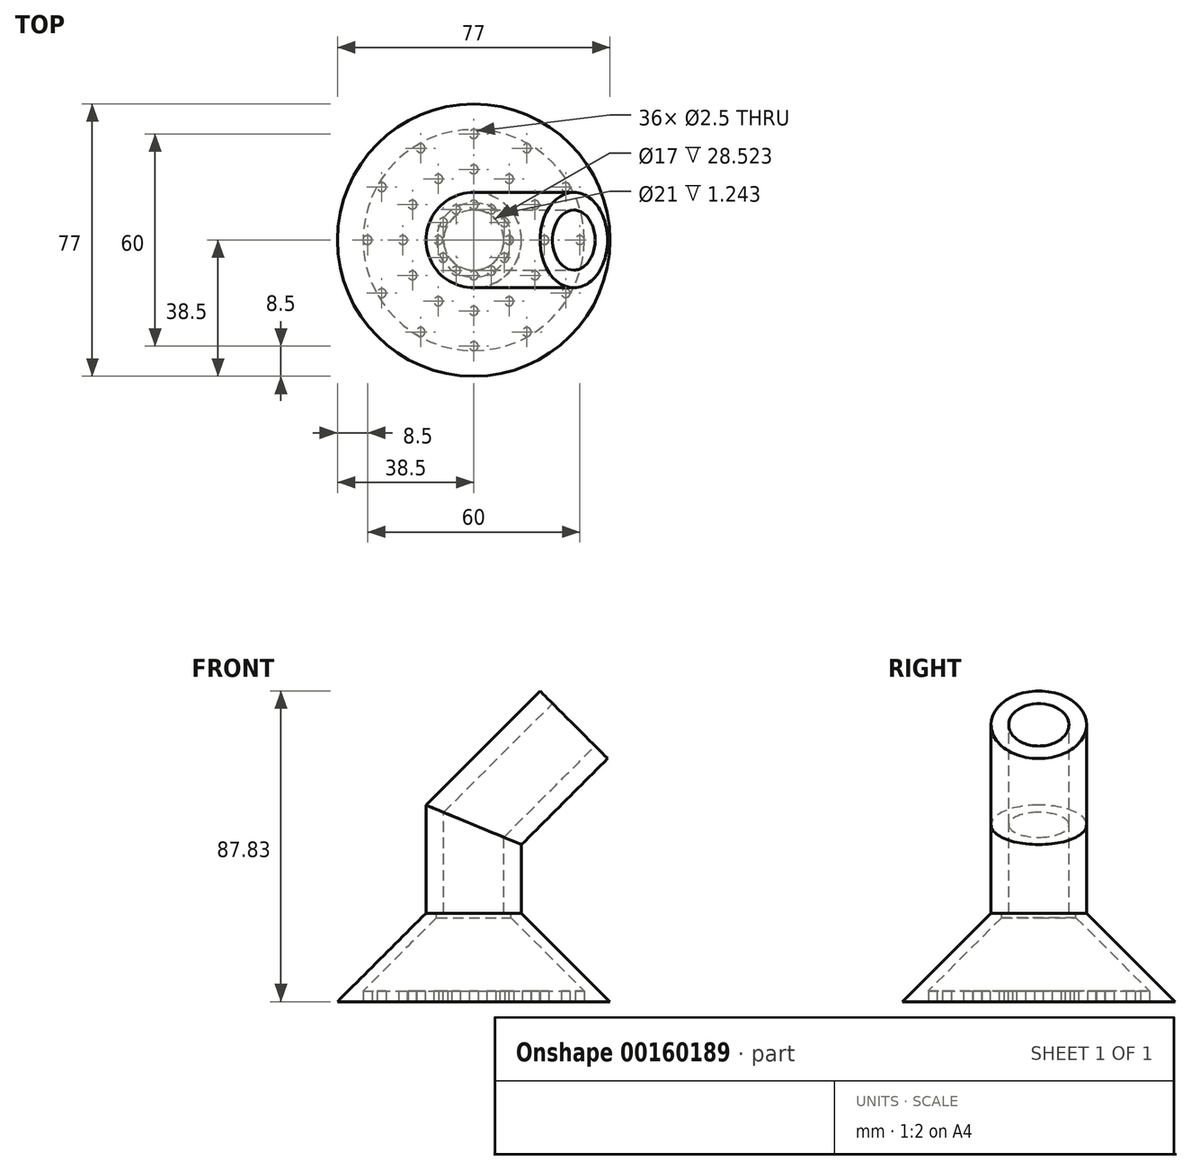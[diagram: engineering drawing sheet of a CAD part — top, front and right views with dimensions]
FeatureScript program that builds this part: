
annotation { "Feature Type Name" : "Feature", "Feature Type Description" : "" }
export const myFeature = defineFeature(function(context is Context, id is Id, definition is map)
    precondition{}
    {
        {
            var Q0;
            Q0=qCreatedBy(makeId("Top.planeOp"),FACE);
            var sketch = newSketch(context, id + "F0", { "sketchPlane" : qUnion([Q0])});
            skCircle(sketch, "E0", {"center": v(0, 0) * mm, "radius": 8.5 * mm});
            skCircle(sketch, "E1.0", {"center": v(0, 0) * mm, "radius": 13.5 * mm});
            skSolve(sketch);
        }
        {
            var Q0;
            Q0=qCreatedBy(makeId("Front.planeOp"),FACE);
            var sketch = newSketch(context, id + "F1", { "sketchPlane" : qUnion([Q0])});
            skLineSegment(sketch, "E2", {"start": v(0, 0) * mm, "end": v(0, 25) * mm});
            skLineSegment(sketch, "E3", {"start": v(0, 25) * mm, "end": v(28.28, 53.28) * mm});
            skSolve(sketch);
        }
        {
            var Q0;
            Q0=makeQuery(id+"F0.imprint","IMPRINT",FACE,{"disambiguationData":[TD([[makeQuery(id+"F0.imprint","IMPRINT",EDGE,{"derivedFrom":sQuery(id+"F0.wireOp",EDGE,"E0")}),-1.0]])]});
            var Q1;
            Q1=sQuery(id+"F1.wireOp",EDGE,"E2");
            var Q2;
            Q2=sQuery(id+"F1.wireOp",EDGE,"E3");
            sweep(context, id + "F10", {"profiles" : qUnion([Q0]), "path" : qUnion([Q1, Q2])});
        }
        {
            var Q0;
            Q0=makeQuery(id+"F10.opSweep","CAP_FACE",FACE,{"disambiguationData":[OSD([sQuery(id+"F0.wireOp",EDGE,"E0"),sQuery(id+"F0.wireOp",EDGE,"E1.0"),sQuery(id+"F1.wireOp",VERTEX,"E2.start")])],"isStart":true});
            var sketch = newSketch(context, id + "F11", { "sketchPlane" : qUnion([Q0])});
            skCircle(sketch, "E4", {"center": v(0, 0) * mm, "radius": 13.5 * mm});
            skSolve(sketch);
        }
        {
            var Q0;
            Q0 = qSketchRegion(id + "F11", true);
            extrude(context, id + "F2", {"entities" : qUnion([Q0]), "operationType" : NewBodyOperationType.ADD, "depth" : 25 * mm, "hasDraft" : true, "draftAngle" : 45 * degree});
        }
        {
            var Q0;
            Q0=makeQuery(id+"F2.opExtrude","CAP_FACE",FACE,{"disambiguationData":[OSD([sQuery(id+"F11.wireOp",EDGE,"E4")])],"isStart":true});
            shell(context, id + "F3", {"entities" : qUnion([Q0]), "thickness" : 3 * mm});
        }
        {
            var Q0;
            Q0=makeQuery(id+"F2.opExtrude","CAP_FACE",FACE,{"disambiguationData":[OSD([sQuery(id+"F11.wireOp",EDGE,"E4")])],"isStart":false});
            var sketch = newSketch(context, id + "F4", { "sketchPlane" : qUnion([Q0])});
            skPoint(sketch, "E5", {"position": v(-10, 0) * mm});
            skPoint(sketch, "E6", {"position": v(-20, 0) * mm});
            skPoint(sketch, "E7", {"position": v(-30, 0) * mm});
            skPoint(sketch, "E8.center", {"position": v(0, 0) * mm});
            skCircle(sketch, "E9", {"center": v(-10, 0) * mm, "radius": 1.25 * mm});
            skCircle(sketch, "E10", {"center": v(-20, 0) * mm, "radius": 1.25 * mm});
            skCircle(sketch, "E11", {"center": v(-30, 0) * mm, "radius": 1.25 * mm});
            skSolve(sketch);
        }
        {
            var Q0;
            Q0=makeQuery(id+"F4.imprint","IMPRINT",FACE,{"disambiguationData":[TD([[makeQuery(id+"F4.imprint","IMPRINT",EDGE,{"derivedFrom":sQuery(id+"F4.wireOp",EDGE,"E9")}),1.0]])]});
            extrude(context, id + "F5", {"entities" : qUnion([Q0]), "endBound" : BoundingType.UP_TO_NEXT, "oppositeDirection" : true, "depth" : 25 * mm});
        }
        {
            var Q0;
            Q0=makeQuery(id+"F4.imprint","IMPRINT",FACE,{"disambiguationData":[TD([[makeQuery(id+"F4.imprint","IMPRINT",EDGE,{"derivedFrom":sQuery(id+"F4.wireOp",EDGE,"E10")}),1.0]])]});
            extrude(context, id + "F6", {"entities" : qUnion([Q0]), "endBound" : BoundingType.UP_TO_NEXT, "oppositeDirection" : true, "depth" : 25 * mm});
        }
        {
            var Q0;
            Q0=makeQuery(id+"F4.imprint","IMPRINT",FACE,{"disambiguationData":[TD([[makeQuery(id+"F4.imprint","IMPRINT",EDGE,{"derivedFrom":sQuery(id+"F4.wireOp",EDGE,"E11")}),1.0]])]});
            extrude(context, id + "F12", {"entities" : qUnion([Q0]), "endBound" : BoundingType.UP_TO_NEXT, "oppositeDirection" : true, "depth" : 25 * mm});
        }
        {
            var Q0;
            Q0=makeQuery(id+"F5.opExtrude","SWEPT_BODY",BODY,{"disambiguationData":[OSD([sQuery(id+"F4.wireOp",EDGE,"E9")])]});
            var Q1;
            Q1=makeQuery(id+"F2.opExtrude","CAP_EDGE",EDGE,{"disambiguationData":[OSD([sQuery(id+"F11.wireOp",EDGE,"E4")])],"isStart":false});
            circularPattern(context, id + "F7", {"operationType" : NewBodyOperationType.REMOVE, "entities" : qUnion([Q0]), "axis" : qUnion([Q1]), "angle" : 30 * degree, "instanceCount" : 15, "oppositeDirection" : true});
        }
        {
            var Q0;
            Q0=makeQuery(id+"F6.opExtrude","SWEPT_BODY",BODY,{"disambiguationData":[OSD([sQuery(id+"F4.wireOp",EDGE,"E10")])]});
            var Q1;
            Q1=makeQuery(id+"F2.opExtrude","CAP_EDGE",EDGE,{"disambiguationData":[OSD([sQuery(id+"F11.wireOp",EDGE,"E4")])],"isStart":false});
            circularPattern(context, id + "F8", {"operationType" : NewBodyOperationType.REMOVE, "entities" : qUnion([Q0]), "axis" : qUnion([Q1]), "angle" : 30 * degree, "instanceCount" : 15});
        }
        {
            var Q0;
            Q0=makeQuery(id+"F12.opExtrude","SWEPT_BODY",BODY,{"disambiguationData":[OSD([sQuery(id+"F4.wireOp",EDGE,"E11")])]});
            var Q1;
            Q1=makeQuery(id+"F2.opExtrude","CAP_EDGE",EDGE,{"disambiguationData":[OSD([sQuery(id+"F11.wireOp",EDGE,"E4")])],"isStart":false});
            circularPattern(context, id + "F9", {"operationType" : NewBodyOperationType.REMOVE, "entities" : qUnion([Q0]), "axis" : qUnion([Q1]), "angle" : 30 * degree, "instanceCount" : 20, "oppositeDirection" : true});
        }
    });
